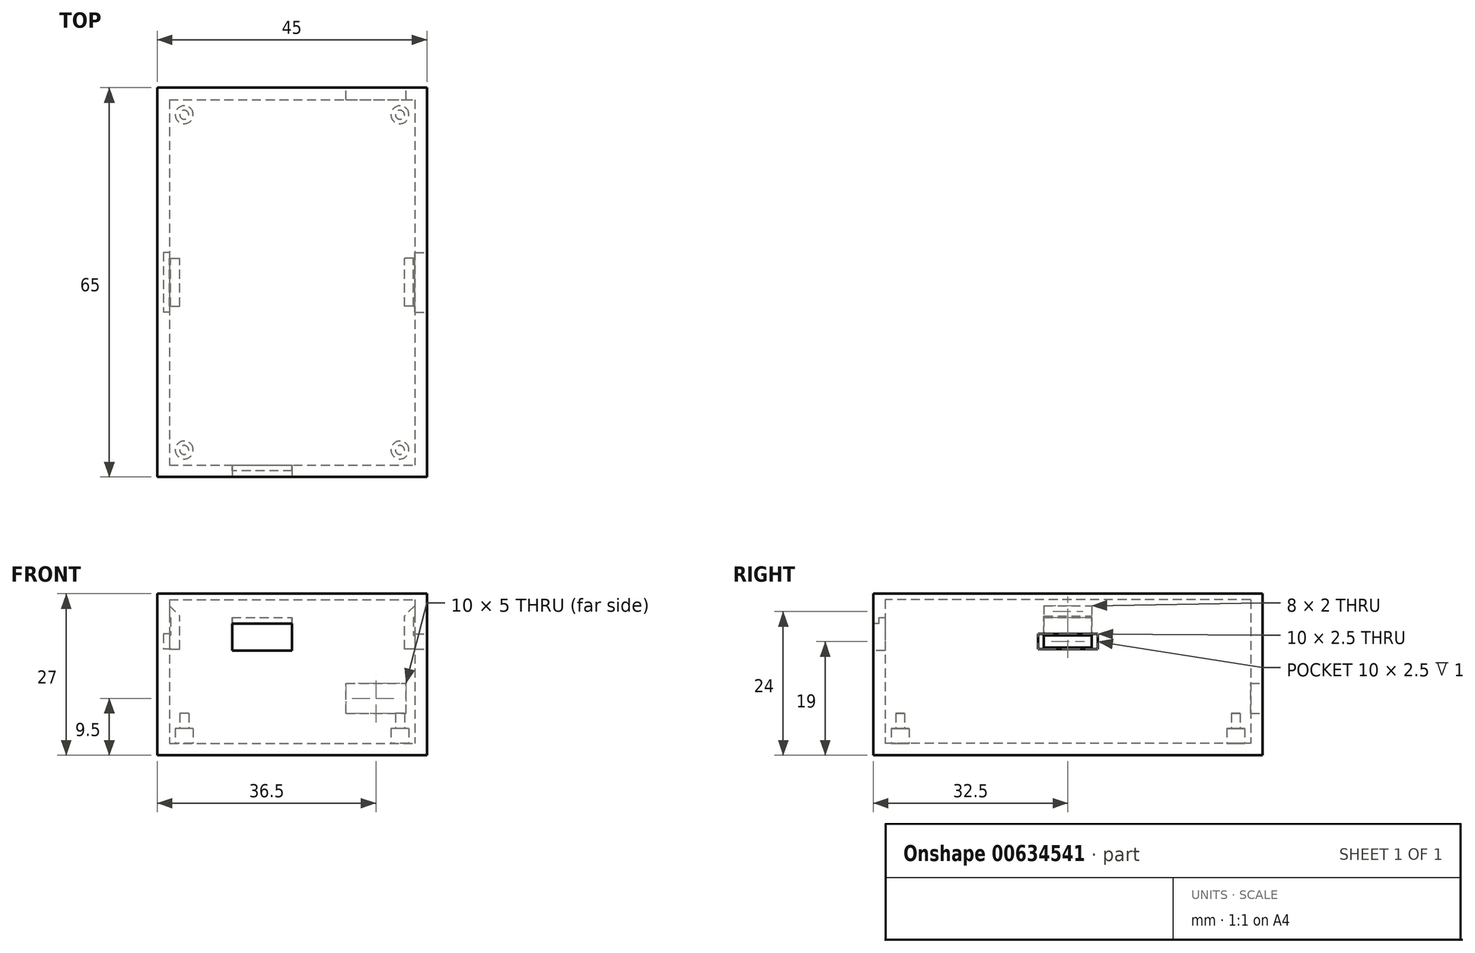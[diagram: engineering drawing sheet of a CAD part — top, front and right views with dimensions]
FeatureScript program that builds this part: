
annotation { "Feature Type Name" : "Feature", "Feature Type Description" : "" }
export const myFeature = defineFeature(function(context is Context, id is Id, definition is map)
    precondition{}
    {
        {
            var Q0;
            Q0=qCreatedBy(makeId("Top.planeOp"),FACE);
            var sketch = newSketch(context, id + "F0", { "sketchPlane" : qUnion([Q0])});
            skLineSegment(sketch, "E0.bottom", {"start": v(22.5, 32.5) * mm, "end": v(-22.5, 32.5) * mm});
            skLineSegment(sketch, "E0.top", {"start": v(22.5, -32.5) * mm, "end": v(-22.5, -32.5) * mm});
            skLineSegment(sketch, "E0.left", {"start": v(22.5, 32.5) * mm, "end": v(22.5, -32.5) * mm});
            skLineSegment(sketch, "E0.right", {"start": v(-22.5, 32.5) * mm, "end": v(-22.5, -32.5) * mm});
            skPoint(sketch, "E0.middle", {"position": v(0, 0) * mm});
            skSolve(sketch);
        }
        {
            var Q0;
            Q0=makeQuery(id+"F0.imprint","IMPRINT",FACE,{"disambiguationData":[TD([[makeQuery(id+"F0.imprint","IMPRINT",EDGE,{"derivedFrom":sQuery(id+"F0.wireOp",EDGE,"E0.bottom")}),1.0]])]});
            extrude(context, id + "F1", {"entities" : qUnion([Q0]), "depth" : 2 * mm, "offsetDistance" : 25 * mm});
        }
        {
            var Q0;
            Q0=makeQuery(id+"F1.opExtrude","CAP_FACE",FACE,{"disambiguationData":[OSD([sQuery(id+"F0.wireOp",EDGE,"E0.bottom"),sQuery(id+"F0.wireOp",EDGE,"E0.top"),sQuery(id+"F0.wireOp",EDGE,"E0.left"),sQuery(id+"F0.wireOp",EDGE,"E0.right")])],"isStart":false});
            var sketch = newSketch(context, id + "F2", { "sketchPlane" : qUnion([Q0])});
            skLineSegment(sketch, "E1.bottom", {"start": v(-20.5, 30.5) * mm, "end": v(20.5, 30.5) * mm});
            skLineSegment(sketch, "E1.top", {"start": v(-20.5, -30.5) * mm, "end": v(20.5, -30.5) * mm});
            skLineSegment(sketch, "E1.left", {"start": v(-20.5, 30.5) * mm, "end": v(-20.5, -30.5) * mm});
            skLineSegment(sketch, "E1.right", {"start": v(20.5, 30.5) * mm, "end": v(20.5, -30.5) * mm});
            skPoint(sketch, "E1.middle", {"position": v(0, 0) * mm});
            skSolve(sketch);
        }
        {
            var Q0;
            Q0=makeQuery(id+"F2.imprint","IMPRINT",FACE,{"disambiguationData":[TD([[makeQuery(id+"F2.imprint","IMPRINT",EDGE,{"derivedFrom":sQuery(id+"F2.wireOp",EDGE,"E1.bottom")}),1.0]])]});
            extrude(context, id + "F3", {"entities" : qUnion([Q0]), "operationType" : NewBodyOperationType.ADD, "depth" : 20 * mm, "offsetDistance" : 25 * mm});
        }
        {
            var Q0;
            Q0=makeQuery(id+"F1.opExtrude","CAP_FACE",FACE,{"disambiguationData":[OSD([sQuery(id+"F0.wireOp",EDGE,"E0.bottom"),sQuery(id+"F0.wireOp",EDGE,"E0.top"),sQuery(id+"F0.wireOp",EDGE,"E0.left"),sQuery(id+"F0.wireOp",EDGE,"E0.right")])],"isStart":false});
            var sketch = newSketch(context, id + "F4", { "sketchPlane" : qUnion([Q0])});
            skCircle(sketch, "E2", {"center": v(-18, 28) * mm, "radius": 0.75 * mm});
            skCircle(sketch, "E3.0.1.0", {"center": v(-18, -28) * mm, "radius": 0.75 * mm});
            skCircle(sketch, "E3.1.0.0", {"center": v(18, 28) * mm, "radius": 0.75 * mm});
            skCircle(sketch, "E3.1.1.0", {"center": v(18, -28) * mm, "radius": 0.75 * mm});
            skLineSegment(sketch, "E3.direction1", {"start": v(-18, 28) * mm, "end": v(18, 28) * mm, "construction": true});
            skLineSegment(sketch, "E3.direction2", {"start": v(-18, 28) * mm, "end": v(-18, -28) * mm, "construction": true});
            skSolve(sketch);
        }
        {
            var Q0;
            Q0 = qSketchRegion(id + "F4", true);
            extrude(context, id + "F5", {"entities" : qUnion([Q0]), "operationType" : NewBodyOperationType.ADD, "depth" : 5 * mm, "offsetDistance" : 25 * mm});
        }
        {
            var Q0;
            Q0=makeQuery(id+"F1.opExtrude","CAP_FACE",FACE,{"disambiguationData":[OSD([sQuery(id+"F0.wireOp",EDGE,"E0.bottom"),sQuery(id+"F0.wireOp",EDGE,"E0.top"),sQuery(id+"F0.wireOp",EDGE,"E0.left"),sQuery(id+"F0.wireOp",EDGE,"E0.right")])],"isStart":false});
            var sketch = newSketch(context, id + "F6", { "sketchPlane" : qUnion([Q0])});
            skCircle(sketch, "E4", {"center": v(-18, 28) * mm, "radius": 1.5 * mm});
            skCircle(sketch, "E5.0.1.0", {"center": v(-18, -28) * mm, "radius": 1.5 * mm});
            skCircle(sketch, "E5.1.0.0", {"center": v(18, 28) * mm, "radius": 1.5 * mm});
            skCircle(sketch, "E5.1.1.0", {"center": v(18, -28) * mm, "radius": 1.5 * mm});
            skLineSegment(sketch, "E5.direction1", {"start": v(-18, 28) * mm, "end": v(18, 28) * mm, "construction": true});
            skLineSegment(sketch, "E5.direction2", {"start": v(-18, 28) * mm, "end": v(-18, -28) * mm, "construction": true});
            skSolve(sketch);
        }
        {
            var Q0;
            Q0 = qSketchRegion(id + "F6", true);
            extrude(context, id + "F7", {"entities" : qUnion([Q0]), "operationType" : NewBodyOperationType.ADD, "depth" : 2.5 * mm, "offsetDistance" : 25 * mm});
        }
        {
            var Q0;
            {var subQ0=sQuery(id+"F0.wireOp",EDGE,"E0.top");Q0=makeQuery(id+"F3.boolean.opBoolean","MERGE",FACE,{"derivedFrom":[makeQuery(id+"F1.opExtrude","SWEPT_FACE",FACE,{"disambiguationData":[OSD([subQ0])]}),makeQuery(id+"F3.opExtrude","SWEPT_FACE",FACE,{"disambiguationData":[OSD([subQ0])]})]});}
            var sketch = newSketch(context, id + "F8", { "sketchPlane" : qUnion([Q0])});
            skLineSegment(sketch, "E6.bottom", {"start": v(-10, 22) * mm, "end": v(0, 22) * mm});
            skLineSegment(sketch, "E6.top", {"start": v(-10, 17.5) * mm, "end": v(0, 17.5) * mm});
            skLineSegment(sketch, "E6.left", {"start": v(-10, 22) * mm, "end": v(-10, 17.5) * mm});
            skLineSegment(sketch, "E6.right", {"start": v(0, 22) * mm, "end": v(0, 17.5) * mm});
            skSolve(sketch);
        }
        {
            var Q0;
            Q0=makeQuery(id+"F8.imprint","IMPRINT",FACE,{"disambiguationData":[TD([[makeQuery(id+"F8.imprint","IMPRINT",EDGE,{"derivedFrom":sQuery(id+"F8.wireOp",EDGE,"E6.bottom")}),1.0]])]});
            extrude(context, id + "F9", {"entities" : qUnion([Q0]), "operationType" : NewBodyOperationType.REMOVE, "endBound" : BoundingType.UP_TO_NEXT, "oppositeDirection" : true, "depth" : 25 * mm, "offsetDistance" : 25 * mm});
        }
        {
            var Q0;
            {var subQ0=sQuery(id+"F0.wireOp",EDGE,"E0.bottom");Q0=makeQuery(id+"F3.boolean.opBoolean","MERGE",FACE,{"derivedFrom":[makeQuery(id+"F1.opExtrude","SWEPT_FACE",FACE,{"disambiguationData":[OSD([subQ0])]}),makeQuery(id+"F3.opExtrude","SWEPT_FACE",FACE,{"disambiguationData":[OSD([subQ0])]})]});}
            var sketch = newSketch(context, id + "F10", { "sketchPlane" : qUnion([Q0])});
            skLineSegment(sketch, "E7.bottom", {"start": v(-19, 12) * mm, "end": v(-9, 12) * mm});
            skLineSegment(sketch, "E7.top", {"start": v(-19, 7) * mm, "end": v(-9, 7) * mm});
            skLineSegment(sketch, "E7.left", {"start": v(-19, 12) * mm, "end": v(-19, 7) * mm});
            skLineSegment(sketch, "E7.right", {"start": v(-9, 12) * mm, "end": v(-9, 7) * mm});
            skSolve(sketch);
        }
        {
            var Q0;
            Q0=makeQuery(id+"F10.imprint","IMPRINT",FACE,{"disambiguationData":[TD([[makeQuery(id+"F10.imprint","IMPRINT",EDGE,{"derivedFrom":sQuery(id+"F10.wireOp",EDGE,"E7.bottom")}),-1.0]])]});
            extrude(context, id + "F11", {"entities" : qUnion([Q0]), "operationType" : NewBodyOperationType.REMOVE, "endBound" : BoundingType.UP_TO_NEXT, "oppositeDirection" : true, "depth" : 25 * mm, "offsetDistance" : 25 * mm});
        }
        {
            var Q0;
            Q0=makeQuery(id+"F3.opExtrude","SWEPT_FACE",FACE,{"disambiguationData":[OSD([sQuery(id+"F2.wireOp",EDGE,"E1.top")])]});
            var sketch = newSketch(context, id + "F12", { "sketchPlane" : qUnion([Q0])});
            skLineSegment(sketch, "E8.bottom", {"start": v(20.5, 22) * mm, "end": v(21.5, 22) * mm});
            skLineSegment(sketch, "E8.top", {"start": v(20.5, 23) * mm, "end": v(21.5, 23) * mm});
            skLineSegment(sketch, "E8.left", {"start": v(20.5, 22) * mm, "end": v(20.5, 23) * mm});
            skLineSegment(sketch, "E8.right", {"start": v(21.5, 22) * mm, "end": v(21.5, 23) * mm});
            skSolve(sketch);
        }
        {
            var Q0;
            Q0=makeQuery(id+"F12.imprint","IMPRINT",FACE,{"disambiguationData":[TD([[makeQuery(id+"F12.imprint","IMPRINT",EDGE,{"derivedFrom":sQuery(id+"F12.wireOp",EDGE,"E8.bottom")}),1.0]])]});
            var Q1;
            Q1=makeQuery(id+"F3.opExtrude","CAP_EDGE",EDGE,{"disambiguationData":[OSD([sQuery(id+"F2.wireOp",EDGE,"E1.left")])],"isStart":false});
            var Q2;
            Q2=makeQuery(id+"F3.opExtrude","CAP_EDGE",EDGE,{"disambiguationData":[OSD([sQuery(id+"F2.wireOp",EDGE,"E1.bottom")])],"isStart":false});
            var Q3;
            Q3=makeQuery(id+"F3.opExtrude","CAP_EDGE",EDGE,{"disambiguationData":[OSD([sQuery(id+"F2.wireOp",EDGE,"E1.right")])],"isStart":false});
            var Q4;
            {var subQ0=sQuery(id+"F2.wireOp",EDGE,"E1.right");var subQ1=sQuery(id+"F2.wireOp",EDGE,"E1.top");Q4=makeQuery(id+"F9.boolean.opBoolean","SPLIT",EDGE,{"disambiguationData":[TD([makeQuery(id+"F3.opExtrude","SWEPT_FACE",FACE,{"disambiguationData":[OSD([subQ0])]})])],"derivedFrom":makeQuery(id+"F3.opExtrude","CAP_EDGE",EDGE,{"disambiguationData":[OSD([subQ1])],"isStart":false})});}
            var Q5;
            {var subQ0=sQuery(id+"F2.wireOp",EDGE,"E1.left");var subQ1=sQuery(id+"F2.wireOp",EDGE,"E1.top");Q5=makeQuery(id+"F9.boolean.opBoolean","SPLIT",EDGE,{"disambiguationData":[TD([makeQuery(id+"F3.opExtrude","SWEPT_FACE",FACE,{"disambiguationData":[OSD([subQ0])]})])],"derivedFrom":makeQuery(id+"F3.opExtrude","CAP_EDGE",EDGE,{"disambiguationData":[OSD([subQ1])],"isStart":false})});}
            sweep(context, id + "F13", {"operationType" : NewBodyOperationType.ADD, "profiles" : qUnion([Q0]), "path" : qUnion([Q1, Q2, Q3, Q4, Q5])});
        }
        {
            var Q0;
            Q0=makeQuery(id+"F3.opExtrude","CAP_FACE",FACE,{"disambiguationData":[OSD([sQuery(id+"F0.wireOp",EDGE,"E0.bottom"),sQuery(id+"F0.wireOp",EDGE,"E0.top"),sQuery(id+"F0.wireOp",EDGE,"E0.left"),sQuery(id+"F0.wireOp",EDGE,"E0.right"),sQuery(id+"F2.wireOp",EDGE,"E1.bottom"),sQuery(id+"F2.wireOp",EDGE,"E1.top"),sQuery(id+"F2.wireOp",EDGE,"E1.left"),sQuery(id+"F2.wireOp",EDGE,"E1.right")])],"isStart":false});
            var sketch = newSketch(context, id + "F14", { "sketchPlane" : qUnion([Q0])});
            skLineSegment(sketch, "E9.bottom", {"start": v(-22.5, 32.5) * mm, "end": v(22.5, 32.5) * mm});
            skLineSegment(sketch, "E9.top", {"start": v(-22.5, -32.5) * mm, "end": v(22.5, -32.5) * mm});
            skLineSegment(sketch, "E9.left", {"start": v(-22.5, 32.5) * mm, "end": v(-22.5, -32.5) * mm});
            skLineSegment(sketch, "E9.right", {"start": v(22.5, 32.5) * mm, "end": v(22.5, -32.5) * mm});
            skLineSegment(sketch, "E10.bottom", {"start": v(21.5, -31.5) * mm, "end": v(-21.5, -31.5) * mm});
            skLineSegment(sketch, "E10.top", {"start": v(21.5, 31.5) * mm, "end": v(-21.5, 31.5) * mm});
            skLineSegment(sketch, "E10.left", {"start": v(21.5, -31.5) * mm, "end": v(21.5, 31.5) * mm});
            skLineSegment(sketch, "E10.right", {"start": v(-21.5, -31.5) * mm, "end": v(-21.5, 31.5) * mm});
            skSolve(sketch);
        }
        {
            var Q0;
            Q0 = qSketchRegion(id + "F14", true);
            extrude(context, id + "F15", {"entities" : qUnion([Q0]), "depth" : 1 * mm, "offsetDistance" : 25 * mm});
        }
        {
            var Q0;
            Q0=makeQuery(id+"F15.opExtrude","CAP_FACE",FACE,{"disambiguationData":[OSD([sQuery(id+"F14.wireOp",EDGE,"E9.bottom"),sQuery(id+"F14.wireOp",EDGE,"E9.top"),sQuery(id+"F14.wireOp",EDGE,"E9.left"),sQuery(id+"F14.wireOp",EDGE,"E9.right"),sQuery(id+"F14.wireOp",EDGE,"E10.bottom"),sQuery(id+"F14.wireOp",EDGE,"E10.top"),sQuery(id+"F14.wireOp",EDGE,"E10.left"),sQuery(id+"F14.wireOp",EDGE,"E10.right")])],"isStart":false});
            var sketch = newSketch(context, id + "F16", { "sketchPlane" : qUnion([Q0])});
            skLineSegment(sketch, "E11.bottom", {"start": v(-22.5, -32.5) * mm, "end": v(22.5, -32.5) * mm});
            skLineSegment(sketch, "E11.top", {"start": v(-22.5, 32.5) * mm, "end": v(22.5, 32.5) * mm});
            skLineSegment(sketch, "E11.left", {"start": v(-22.5, -32.5) * mm, "end": v(-22.5, 32.5) * mm});
            skLineSegment(sketch, "E11.right", {"start": v(22.5, -32.5) * mm, "end": v(22.5, 32.5) * mm});
            skLineSegment(sketch, "E12.0", {"start": v(-20.5, 30.5) * mm, "end": v(20.5, 30.5) * mm});
            skLineSegment(sketch, "E12.1", {"start": v(-20.5, -30.5) * mm, "end": v(-20.5, 30.5) * mm});
            skLineSegment(sketch, "E12.2", {"start": v(-20.5, -30.5) * mm, "end": v(20.5, -30.5) * mm});
            skLineSegment(sketch, "E12.3", {"start": v(20.5, -30.5) * mm, "end": v(20.5, 30.5) * mm});
            skSolve(sketch);
        }
        {
            var Q0;
            Q0 = qSketchRegion(id + "F16", true);
            extrude(context, id + "F17", {"entities" : qUnion([Q0]), "operationType" : NewBodyOperationType.ADD, "depth" : 4 * mm, "offsetDistance" : 25 * mm});
        }
        {
            var Q0;
            Q0=makeQuery(id+"F17.opExtrude","SWEPT_FACE",FACE,{"disambiguationData":[OSD([sQuery(id+"F16.wireOp",EDGE,"E12.2")])]});
            var sketch = newSketch(context, id + "F18", { "sketchPlane" : qUnion([Q0])});
            skLineSegment(sketch, "E13.bottom", {"start": v(20.5, 27) * mm, "end": v(-20.5, 27) * mm});
            skLineSegment(sketch, "E13.top", {"start": v(20.5, 26) * mm, "end": v(-20.5, 26) * mm});
            skLineSegment(sketch, "E13.left", {"start": v(20.5, 27) * mm, "end": v(20.5, 26) * mm});
            skLineSegment(sketch, "E13.right", {"start": v(-20.5, 27) * mm, "end": v(-20.5, 26) * mm});
            skSolve(sketch);
        }
        {
            var Q0;
            Q0 = qSketchRegion(id + "F18", true);
            extrude(context, id + "F19", {"entities" : qUnion([Q0]), "operationType" : NewBodyOperationType.ADD, "endBound" : BoundingType.UP_TO_NEXT, "depth" : 25 * mm, "offsetDistance" : 25 * mm});
        }
        {
            var Q0;
            Q0=qCreatedBy(makeId("Front.planeOp"),FACE);
            var sketch = newSketch(context, id + "F20", { "sketchPlane" : qUnion([Q0])});
            skLineSegment(sketch, "E14", {"start": v(-20.5, 25) * mm, "end": v(-20.5, 23) * mm});
            skLineSegment(sketch, "E15", {"start": v(-20.5, 25) * mm, "end": v(-18.75, 23.25) * mm});
            skLineSegment(sketch, "E16", {"start": v(-20.5, 23) * mm, "end": v(-20.25, 23) * mm});
            skLineSegment(sketch, "E17", {"start": v(-20.25, 23) * mm, "end": v(-20.25, 20) * mm});
            skLineSegment(sketch, "E18", {"start": v(-20.25, 20) * mm, "end": v(-21.5, 20) * mm});
            skLineSegment(sketch, "E19", {"start": v(-21.5, 20) * mm, "end": v(-21.5, 19) * mm});
            skLineSegment(sketch, "E20", {"start": v(-21.5, 19) * mm, "end": v(-20.25, 17.75) * mm});
            skLineSegment(sketch, "E21", {"start": v(-20.25, 17.75) * mm, "end": v(-18.75, 17.75) * mm});
            skLineSegment(sketch, "E22", {"start": v(-18.75, 17.75) * mm, "end": v(-18.75, 23.25) * mm});
            skLineSegment(sketch, "E23.MirrorCS", {"start": v(20.5, 23) * mm, "end": v(20.25, 23) * mm});
            skLineSegment(sketch, "E24.MirrorCS", {"start": v(21.5, 20) * mm, "end": v(21.5, 19) * mm});
            skLineSegment(sketch, "E25.MirrorCS", {"start": v(20.25, 17.75) * mm, "end": v(18.75, 17.75) * mm});
            skLineSegment(sketch, "E26.MirrorCS", {"start": v(20.25, 20) * mm, "end": v(21.5, 20) * mm});
            skLineSegment(sketch, "E27.MirrorCS", {"start": v(18.75, 17.75) * mm, "end": v(18.75, 23.25) * mm});
            skLineSegment(sketch, "E28.MirrorCS", {"start": v(21.5, 19) * mm, "end": v(20.25, 17.75) * mm});
            skLineSegment(sketch, "E29.MirrorCS", {"start": v(20.25, 23) * mm, "end": v(20.25, 20) * mm});
            skLineSegment(sketch, "E30.MirrorCS", {"start": v(20.5, 25) * mm, "end": v(20.5, 23) * mm});
            skLineSegment(sketch, "E31.MirrorCS", {"start": v(20.5, 25) * mm, "end": v(18.75, 23.25) * mm});
            skSolve(sketch);
        }
        {
            var Q0;
            Q0 = qSketchRegion(id + "F20", true);
            extrude(context, id + "F21", {"entities" : qUnion([Q0]), "operationType" : NewBodyOperationType.ADD, "endBound" : BoundingType.SYMMETRIC, "depth" : 8 * mm, "offsetDistance" : 25 * mm});
        }
        {
            var Q0;
            Q0=qCreatedBy(makeId("Front.planeOp"),FACE);
            var sketch = newSketch(context, id + "F22", { "sketchPlane" : qUnion([Q0])});
            skLineSegment(sketch, "E32.bottom", {"start": v(-20.5, 20.25) * mm, "end": v(-21.5, 20.25) * mm});
            skLineSegment(sketch, "E32.top", {"start": v(-20.5, 17.75) * mm, "end": v(-21.5, 17.75) * mm});
            skLineSegment(sketch, "E32.left", {"start": v(-20.5, 20.25) * mm, "end": v(-20.5, 17.75) * mm});
            skLineSegment(sketch, "E32.right", {"start": v(-21.5, 20.25) * mm, "end": v(-21.5, 17.75) * mm});
            skSolve(sketch);
        }
        {
            var Q0;
            Q0 = qSketchRegion(id + "F22", true);
            extrude(context, id + "F23", {"entities" : qUnion([Q0]), "operationType" : NewBodyOperationType.REMOVE, "endBound" : BoundingType.SYMMETRIC, "oppositeDirection" : true, "depth" : 10 * mm, "offsetDistance" : 25 * mm});
        }
        {
            var Q0;
            {var subQ0=sQuery(id+"F0.wireOp",EDGE,"E0.left");Q0=makeQuery(id+"F3.boolean.opBoolean","MERGE",FACE,{"derivedFrom":[makeQuery(id+"F1.opExtrude","SWEPT_FACE",FACE,{"disambiguationData":[OSD([subQ0])]}),makeQuery(id+"F3.opExtrude","SWEPT_FACE",FACE,{"disambiguationData":[OSD([subQ0])]})]});}
            var sketch = newSketch(context, id + "F24", { "sketchPlane" : qUnion([Q0])});
            skLineSegment(sketch, "E33.bottom", {"start": v(-5, 20.25) * mm, "end": v(5, 20.25) * mm});
            skLineSegment(sketch, "E33.top", {"start": v(-5, 17.75) * mm, "end": v(5, 17.75) * mm});
            skLineSegment(sketch, "E33.left", {"start": v(-5, 20.25) * mm, "end": v(-5, 17.75) * mm});
            skLineSegment(sketch, "E33.right", {"start": v(5, 20.25) * mm, "end": v(5, 17.75) * mm});
            skSolve(sketch);
        }
        {
            var Q0;
            Q0=makeQuery(id+"F24.imprint","IMPRINT",FACE,{"disambiguationData":[TD([[makeQuery(id+"F24.imprint","IMPRINT",EDGE,{"derivedFrom":sQuery(id+"F24.wireOp",EDGE,"E33.bottom")}),-1.0]])]});
            extrude(context, id + "F25", {"entities" : qUnion([Q0]), "operationType" : NewBodyOperationType.REMOVE, "oppositeDirection" : true, "depth" : 2 * mm, "offsetDistance" : 25 * mm});
        }
    });
